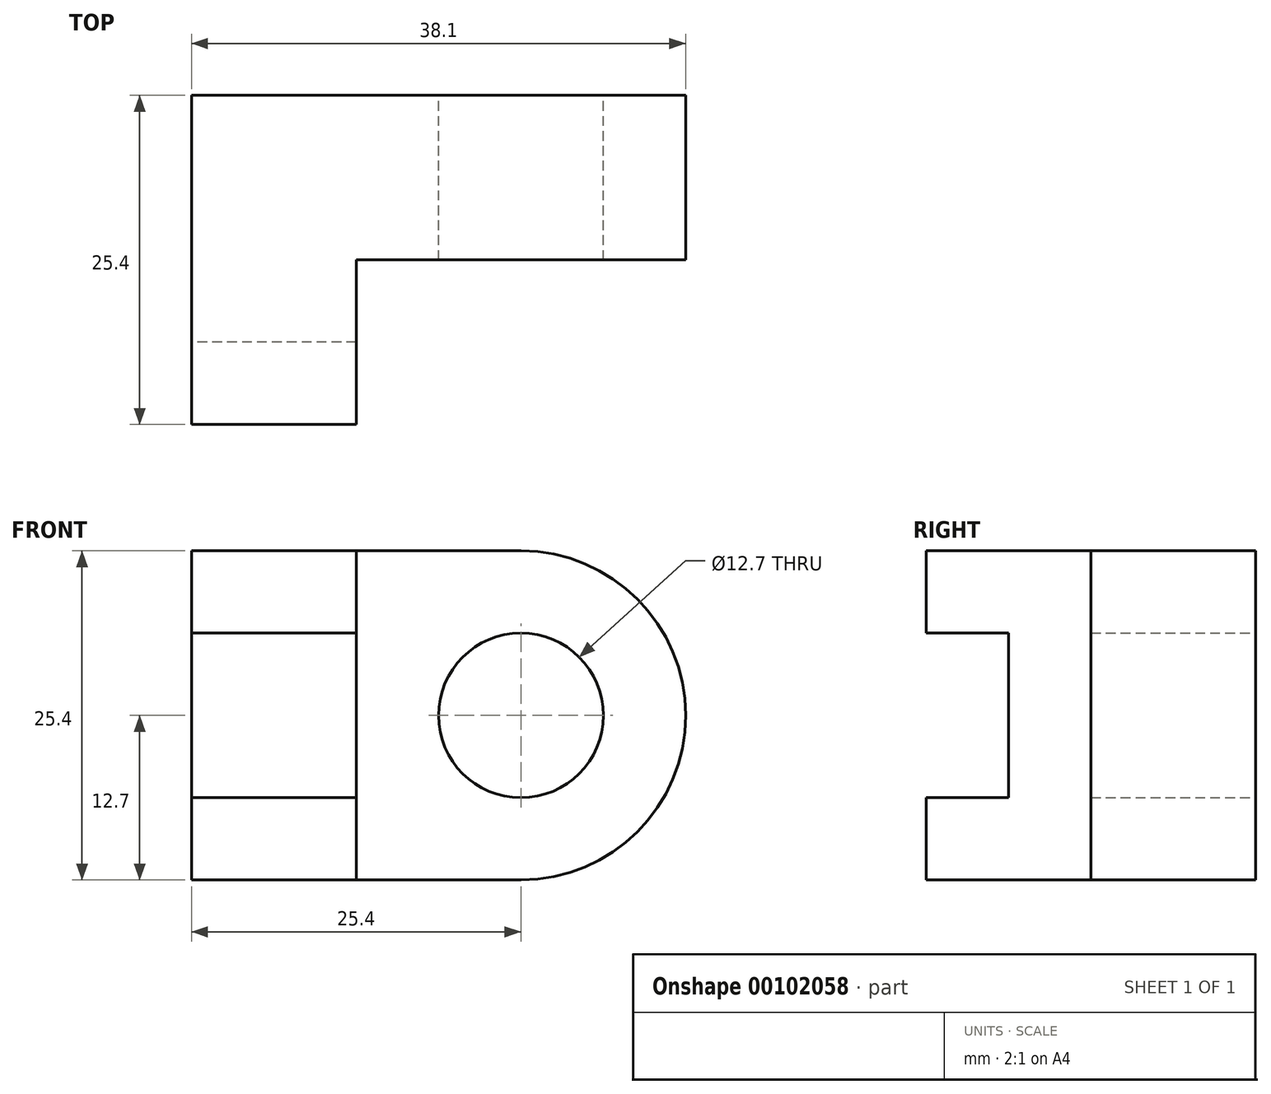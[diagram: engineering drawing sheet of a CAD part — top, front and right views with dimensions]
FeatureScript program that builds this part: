
annotation { "Feature Type Name" : "Feature", "Feature Type Description" : "" }
export const myFeature = defineFeature(function(context is Context, id is Id, definition is map)
    precondition{}
    {
        {
            var Q0;
            Q0=qCreatedBy(makeId("Front.planeOp"),FACE);
            var sketch = newSketch(context, id + "F0", { "sketchPlane" : qUnion([Q0])});
            skLineSegment(sketch, "E0", {"start": v(0, 0) * mm, "end": v(0, 25.4) * mm});
            skLineSegment(sketch, "E1", {"start": v(0, 25.4) * mm, "end": v(25.4, 25.4) * mm});
            skLineSegment(sketch, "E2", {"start": v(0, 0) * mm, "end": v(25.4, 0) * mm});
            skArc(sketch, "E3", {"start": v(25.4, 0) * mm, "mid": v(38.1, 12.7) * mm, "end": v(25.4, 25.4) * mm});
            skCircle(sketch, "E4", {"center": v(25.4, 12.7) * mm, "radius": 6.35 * mm});
            skSolve(sketch);
        }
        {
            var Q0;
            Q0=makeQuery(id+"F0.imprint","IMPRINT",FACE,{"disambiguationData":[TD([[makeQuery(id+"F0.imprint","IMPRINT",EDGE,{"derivedFrom":sQuery(id+"F0.wireOp",EDGE,"E0")}),-1.0]])]});
            extrude(context, id + "F1", {"entities" : qUnion([Q0]), "depth" : 12.7 * mm});
        }
        {
            var Q0;
            Q0=qCreatedBy(makeId("Right.planeOp"),FACE);
            var sketch = newSketch(context, id + "F2", { "sketchPlane" : qUnion([Q0])});
            skLineSegment(sketch, "E5", {"start": v(-12.7, 25.4) * mm, "end": v(-25.4, 25.4) * mm});
            skLineSegment(sketch, "E6", {"start": v(-25.4, 25.4) * mm, "end": v(-25.4, 0) * mm});
            skLineSegment(sketch, "E7", {"start": v(-25.4, 0) * mm, "end": v(-12.7, 0) * mm});
            skLineSegment(sketch, "E8", {"start": v(-12.7, 0) * mm, "end": v(-12.7, 25.4) * mm});
            skLineSegment(sketch, "E9", {"start": v(-25.4, 19.05) * mm, "end": v(-19.05, 19.05) * mm});
            skLineSegment(sketch, "E10", {"start": v(-19.05, 19.05) * mm, "end": v(-19.05, 6.35) * mm});
            skLineSegment(sketch, "E11", {"start": v(-19.05, 6.35) * mm, "end": v(-25.4, 6.35) * mm});
            skSolve(sketch);
        }
        {
            var Q0;
            {var subQ3=sQuery(id+"F2.wireOp",EDGE,"E5");Q0=makeQuery(id+"F2.imprint","IMPRINT",FACE,{"disambiguationData":[TD([[makeQuery(id+"F2.imprint","IMPRINT",EDGE,{"derivedFrom":subQ3}),1.0]])]});}
            extrude(context, id + "F3", {"entities" : qUnion([Q0]), "operationType" : NewBodyOperationType.ADD, "depth" : 12.7 * mm});
        }
    });
